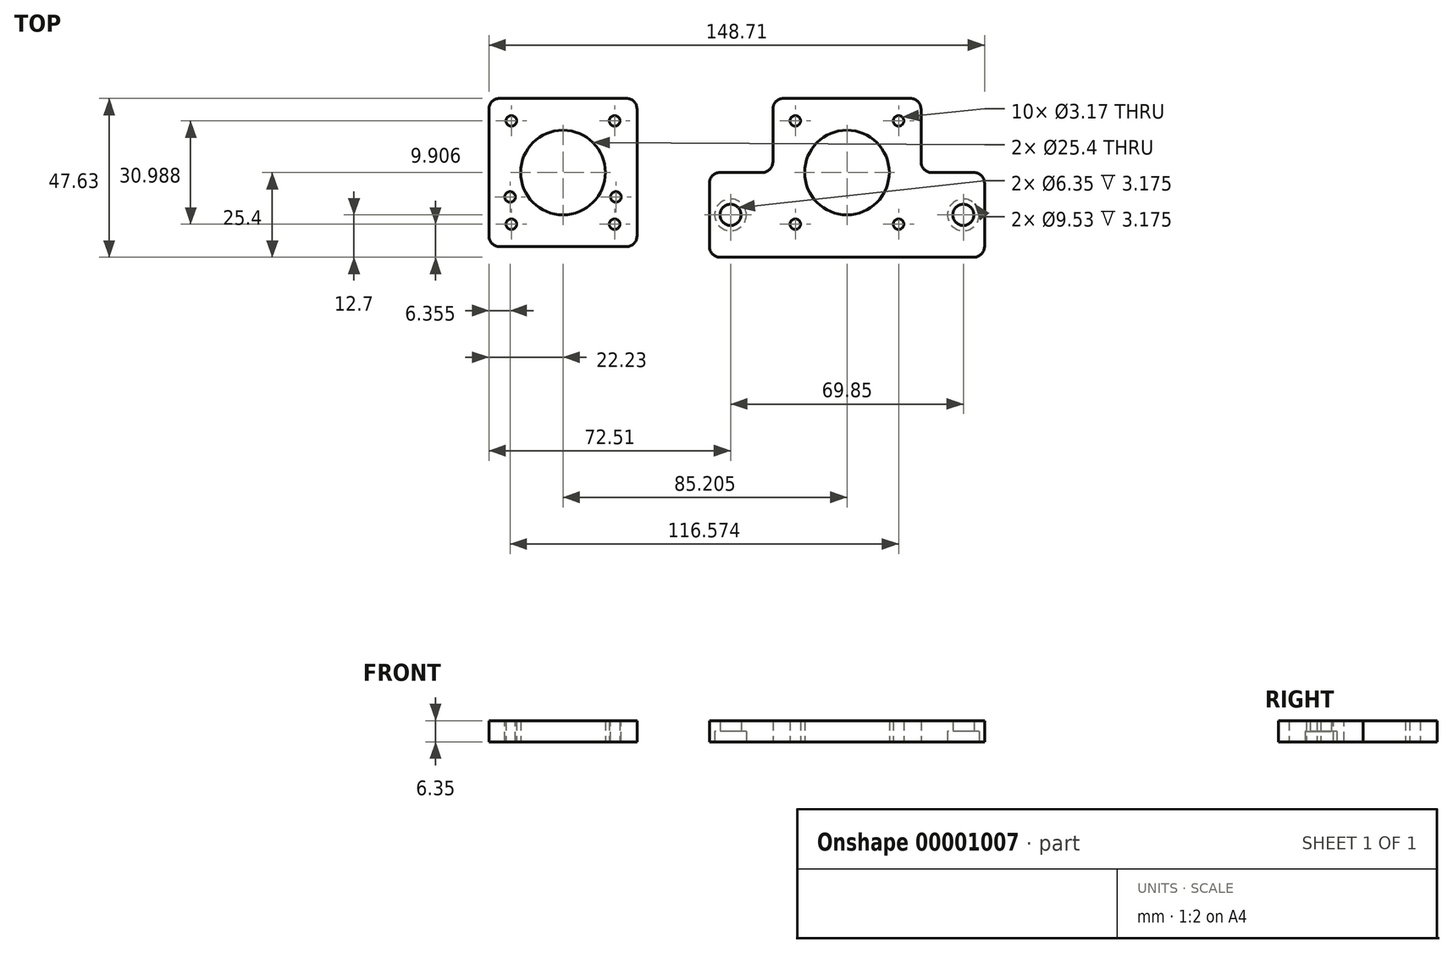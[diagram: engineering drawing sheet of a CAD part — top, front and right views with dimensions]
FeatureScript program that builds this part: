
annotation { "Feature Type Name" : "Feature", "Feature Type Description" : "" }
export const myFeature = defineFeature(function(context is Context, id is Id, definition is map)
    precondition{}
    {
        {
            var Q0;
            Q0=qCreatedBy(makeId("Top.planeOp"),FACE);
            var sketch = newSketch(context, id + "F0", { "sketchPlane" : qUnion([Q0])});
            skLineSegment(sketch, "E0.bottom", {"start": v(-19.05, 22.22) * mm, "end": v(19.05, 22.23) * mm});
            skLineSegment(sketch, "E0.top", {"start": v(-19.05, -22.23) * mm, "end": v(19.05, -22.22) * mm});
            skLineSegment(sketch, "E0.left", {"start": v(-22.23, 19.05) * mm, "end": v(-22.23, -19.05) * mm});
            skLineSegment(sketch, "E0.right", {"start": v(22.23, 19.05) * mm, "end": v(22.23, -19.05) * mm});
            skCircle(sketch, "E1", {"center": v(-15.5, 15.5) * mm, "radius": 1.59 * mm});
            skCircle(sketch, "E2", {"center": v(15.5, 15.5) * mm, "radius": 1.59 * mm});
            skCircle(sketch, "E3", {"center": v(15.5, -15.5) * mm, "radius": 1.59 * mm});
            skCircle(sketch, "E4", {"center": v(-15.5, -15.5) * mm, "radius": 1.59 * mm});
            skCircle(sketch, "E5", {"center": v(0, 0) * mm, "radius": 12.7 * mm});
            skPoint(sketch, "E6.visualSharp", {"position": v(-22.23, 22.22) * mm});
            skArc(sketch, "E6.filletArc", {"start": v(-19.05, 22.22) * mm, "mid": v(-21.3, 21.3) * mm, "end": v(-22.23, 19.05) * mm});
            skPoint(sketch, "E7.visualSharp", {"position": v(22.23, 22.23) * mm});
            skArc(sketch, "E7.filletArc", {"start": v(22.22, 19.05) * mm, "mid": v(21.3, 21.3) * mm, "end": v(19.05, 22.23) * mm});
            skPoint(sketch, "E8.visualSharp", {"position": v(22.22, -22.22) * mm});
            skArc(sketch, "E8.filletArc", {"start": v(19.05, -22.22) * mm, "mid": v(21.3, -21.3) * mm, "end": v(22.23, -19.05) * mm});
            skPoint(sketch, "E9.visualSharp", {"position": v(-22.23, -22.23) * mm});
            skArc(sketch, "E9.filletArc", {"start": v(-22.23, -19.05) * mm, "mid": v(-21.3, -21.3) * mm, "end": v(-19.05, -22.23) * mm});
            skLineSegment(sketch, "E10.bottom", {"start": v(66.16, 22.23) * mm, "end": v(104.26, 22.23) * mm});
            skLineSegment(sketch, "E10.left", {"start": v(62.98, 19.05) * mm, "end": v(62.98, 3.18) * mm});
            skLineSegment(sketch, "E10.right", {"start": v(107.43, 19.05) * mm, "end": v(107.43, 3.18) * mm});
            skPoint(sketch, "E11.visualSharp", {"position": v(62.98, 22.23) * mm});
            skArc(sketch, "E11.filletArc", {"start": v(66.16, 22.23) * mm, "mid": v(63.9, 21.3) * mm, "end": v(62.98, 19.05) * mm});
            skPoint(sketch, "E12.visualSharp", {"position": v(107.43, 22.23) * mm});
            skArc(sketch, "E12.filletArc", {"start": v(107.43, 19.05) * mm, "mid": v(106.5, 21.3) * mm, "end": v(104.26, 22.22) * mm});
            skPoint(sketch, "E13", {"position": v(85.2, -22.23) * mm});
            skCircle(sketch, "E14", {"center": v(85.2, 0) * mm, "radius": 12.7 * mm});
            skCircle(sketch, "E15", {"center": v(69.71, 15.5) * mm, "radius": 1.59 * mm});
            skCircle(sketch, "E16", {"center": v(100.7, 15.5) * mm, "radius": 1.59 * mm});
            skCircle(sketch, "E17", {"center": v(100.7, -15.5) * mm, "radius": 1.59 * mm});
            skCircle(sketch, "E18", {"center": v(69.71, -15.5) * mm, "radius": 1.59 * mm});
            skLineSegment(sketch, "E19", {"start": v(110.6, 0) * mm, "end": v(123.3, 0) * mm});
            skLineSegment(sketch, "E20", {"start": v(126.48, -3.18) * mm, "end": v(126.48, -22.22) * mm});
            skLineSegment(sketch, "E21", {"start": v(123.3, -25.4) * mm, "end": v(47.1, -25.4) * mm});
            skLineSegment(sketch, "E22", {"start": v(43.93, -22.23) * mm, "end": v(43.93, -3.18) * mm});
            skPoint(sketch, "E23.visualSharp", {"position": v(43.93, 0) * mm});
            skArc(sketch, "E23.filletArc", {"start": v(47.1, 0) * mm, "mid": v(44.86, -0.93) * mm, "end": v(43.93, -3.18) * mm});
            skPoint(sketch, "E24.visualSharp", {"position": v(43.93, -25.4) * mm});
            skArc(sketch, "E24.filletArc", {"start": v(43.93, -22.23) * mm, "mid": v(44.86, -24.47) * mm, "end": v(47.1, -25.4) * mm});
            skPoint(sketch, "E25.visualSharp", {"position": v(126.48, -25.4) * mm});
            skArc(sketch, "E25.filletArc", {"start": v(123.3, -25.4) * mm, "mid": v(125.55, -24.47) * mm, "end": v(126.48, -22.22) * mm});
            skPoint(sketch, "E26.visualSharp", {"position": v(126.48, 0) * mm});
            skArc(sketch, "E26.filletArc", {"start": v(126.48, -3.18) * mm, "mid": v(125.55, -0.93) * mm, "end": v(123.3, 0) * mm});
            skArc(sketch, "E27.filletArc", {"start": v(107.43, 3.17) * mm, "mid": v(108.36, 0.93) * mm, "end": v(110.6, 0) * mm});
            skLineSegment(sketch, "E28", {"start": v(47.1, 0) * mm, "end": v(59.8, 0) * mm});
            skPoint(sketch, "E29.visualSharp", {"position": v(62.98, 0) * mm});
            skArc(sketch, "E29.filletArc", {"start": v(59.8, 0) * mm, "mid": v(62.05, 0.93) * mm, "end": v(62.98, 3.17) * mm});
            skLineSegment(sketch, "E30.rect.bottom", {"start": v(56, 29.21) * mm, "end": v(114.42, 29.21) * mm, "construction": true});
            skLineSegment(sketch, "E30.rect.top", {"start": v(56, -29.2) * mm, "end": v(114.42, -29.2) * mm, "construction": true});
            skLineSegment(sketch, "E30.rect.left", {"start": v(56, 29.21) * mm, "end": v(56, -29.2) * mm, "construction": true});
            skLineSegment(sketch, "E30.rect.right", {"start": v(114.42, 29.21) * mm, "end": v(114.42, -29.2) * mm, "construction": true});
            skCircle(sketch, "E31", {"center": v(50.28, -12.7) * mm, "radius": 4.76 * mm});
            skCircle(sketch, "E32", {"center": v(120.13, -12.7) * mm, "radius": 4.76 * mm});
            skCircle(sketch, "E33", {"center": v(50.28, -12.7) * mm, "radius": 3.18 * mm});
            skCircle(sketch, "E34", {"center": v(120.13, -12.7) * mm, "radius": 3.18 * mm});
            skLineSegment(sketch, "E35", {"start": v(85.2, 0) * mm, "end": v(65.64, 0) * mm, "construction": true});
            skSolve(sketch);
        }
        {
            var Q0;
            {Q0=qUnion([makeQuery(id+"F0.imprint","IMPRINT",FACE,{"disambiguationData":[TD([[makeQuery(id+"F0.imprint","IMPRINT",EDGE,{"derivedFrom":sQuery(id+"F0.wireOp",EDGE,"E0.bottom")}),-1.0]])]}),makeQuery(id+"F0.imprint","IMPRINT",FACE,{"disambiguationData":[TD([[makeQuery(id+"F0.imprint","IMPRINT",EDGE,{"derivedFrom":sQuery(id+"F0.wireOp",EDGE,"E10.bottom")}),-1.0]])]})]);}
            var Q1;
            Q1=makeQuery(id+"F0.imprint","IMPRINT",FACE,{"disambiguationData":[TD([[makeQuery(id+"F0.imprint","IMPRINT",EDGE,{"derivedFrom":sQuery(id+"F0.wireOp",EDGE,"E31")}),1.0]])]});
            var Q2;
            Q2=makeQuery(id+"F0.imprint","IMPRINT",FACE,{"disambiguationData":[TD([[makeQuery(id+"F0.imprint","IMPRINT",EDGE,{"derivedFrom":sQuery(id+"F0.wireOp",EDGE,"caab8d64-f1ce-43ae-893e-d7ddbd2fbb18")}),1.0]])]});
            var Q3;
            Q3=makeQuery(id+"F0.imprint","IMPRINT",FACE,{"disambiguationData":[TD([[makeQuery(id+"F0.imprint","IMPRINT",EDGE,{"derivedFrom":sQuery(id+"F0.wireOp",EDGE,"E32")}),1.0]])]});
            var Q4;
            Q4=makeQuery(id+"F0.imprint","IMPRINT",FACE,{"disambiguationData":[TD([[makeQuery(id+"F0.imprint","IMPRINT",EDGE,{"derivedFrom":sQuery(id+"F0.wireOp",EDGE,"5852d22e-677d-4903-8a8a-632ebfd74a16")}),1.0]])]});
            extrude(context, id + "F1", {"entities" : qUnion([Q0, Q1, Q2, Q3, Q4]), "depth" : 6.35 * mm});
        }
        {
            var Q0;
            Q0=makeQuery(id+"F1.opExtrude","CAP_FACE",FACE,{"disambiguationData":[OSD([sQuery(id+"F0.wireOp",EDGE,"E0.bottom"),sQuery(id+"F0.wireOp",EDGE,"E0.top"),sQuery(id+"F0.wireOp",EDGE,"E0.left"),sQuery(id+"F0.wireOp",EDGE,"E0.right"),sQuery(id+"F0.wireOp",EDGE,"E1"),sQuery(id+"F0.wireOp",EDGE,"E2"),sQuery(id+"F0.wireOp",EDGE,"E3"),sQuery(id+"F0.wireOp",EDGE,"E4"),sQuery(id+"F0.wireOp",EDGE,"E5"),sQuery(id+"F0.wireOp",EDGE,"E6.filletArc"),sQuery(id+"F0.wireOp",EDGE,"E7.filletArc"),sQuery(id+"F0.wireOp",EDGE,"E8.filletArc"),sQuery(id+"F0.wireOp",EDGE,"E9.filletArc")])],"isStart":false});
            var sketch = newSketch(context, id + "F2", { "sketchPlane" : qUnion([Q0])});
            skCircle(sketch, "E36", {"center": v(-15.88, -7.32) * mm, "radius": 1.59 * mm});
            skCircle(sketch, "E37", {"center": v(15.88, -7.32) * mm, "radius": 1.59 * mm});
            skSolve(sketch);
        }
        {
            var Q0;
            {Q0=qUnion([makeQuery(id+"F2.imprint","IMPRINT",FACE,{"disambiguationData":[TD([[makeQuery(id+"F2.imprint","IMPRINT",EDGE,{"derivedFrom":sQuery(id+"F2.wireOp",EDGE,"E36")}),1.0]])]}),makeQuery(id+"F2.imprint","IMPRINT",FACE,{"disambiguationData":[TD([[makeQuery(id+"F2.imprint","IMPRINT",EDGE,{"derivedFrom":sQuery(id+"F2.wireOp",EDGE,"E37")}),1.0]])]})]);}
            extrude(context, id + "F3", {"entities" : qUnion([Q0]), "operationType" : NewBodyOperationType.REMOVE, "endBound" : BoundingType.THROUGH_ALL, "oppositeDirection" : true, "depth" : 25.4 * mm});
        }
        {
            var Q0;
            Q0=makeQuery(id+"F0.imprint","IMPRINT",FACE,{"disambiguationData":[TD([[makeQuery(id+"F0.imprint","IMPRINT",EDGE,{"derivedFrom":sQuery(id+"F0.wireOp",EDGE,"E32")}),1.0]])]});
            var Q1;
            Q1=makeQuery(id+"F0.imprint","IMPRINT",FACE,{"disambiguationData":[TD([[makeQuery(id+"F0.imprint","IMPRINT",EDGE,{"derivedFrom":sQuery(id+"F0.wireOp",EDGE,"5852d22e-677d-4903-8a8a-632ebfd74a16")}),1.0]])]});
            var Q2;
            Q2=makeQuery(id+"F0.imprint","IMPRINT",FACE,{"disambiguationData":[TD([[makeQuery(id+"F0.imprint","IMPRINT",EDGE,{"derivedFrom":sQuery(id+"F0.wireOp",EDGE,"E31")}),1.0]])]});
            var Q3;
            Q3=makeQuery(id+"F0.imprint","IMPRINT",FACE,{"disambiguationData":[TD([[makeQuery(id+"F0.imprint","IMPRINT",EDGE,{"derivedFrom":sQuery(id+"F0.wireOp",EDGE,"caab8d64-f1ce-43ae-893e-d7ddbd2fbb18")}),1.0]])]});
            var Q4;
            Q4=sQuery(id+"F0.wireOp",EDGE,"E31");
            var Q5;
            Q5=sQuery(id+"F0.wireOp",EDGE,"caab8d64-f1ce-43ae-893e-d7ddbd2fbb18");
            var Q6;
            Q6=sQuery(id+"F0.wireOp",EDGE,"5852d22e-677d-4903-8a8a-632ebfd74a16");
            var Q7;
            Q7=sQuery(id+"F0.wireOp",EDGE,"E32");
            extrude(context, id + "F4", {"entities" : qUnion([Q0, Q1, Q2, Q3]), "operationType" : NewBodyOperationType.REMOVE, "surfaceEntities" : qUnion([Q4, Q5, Q6, Q7]), "depth" : 3.17 * mm});
        }
    });
